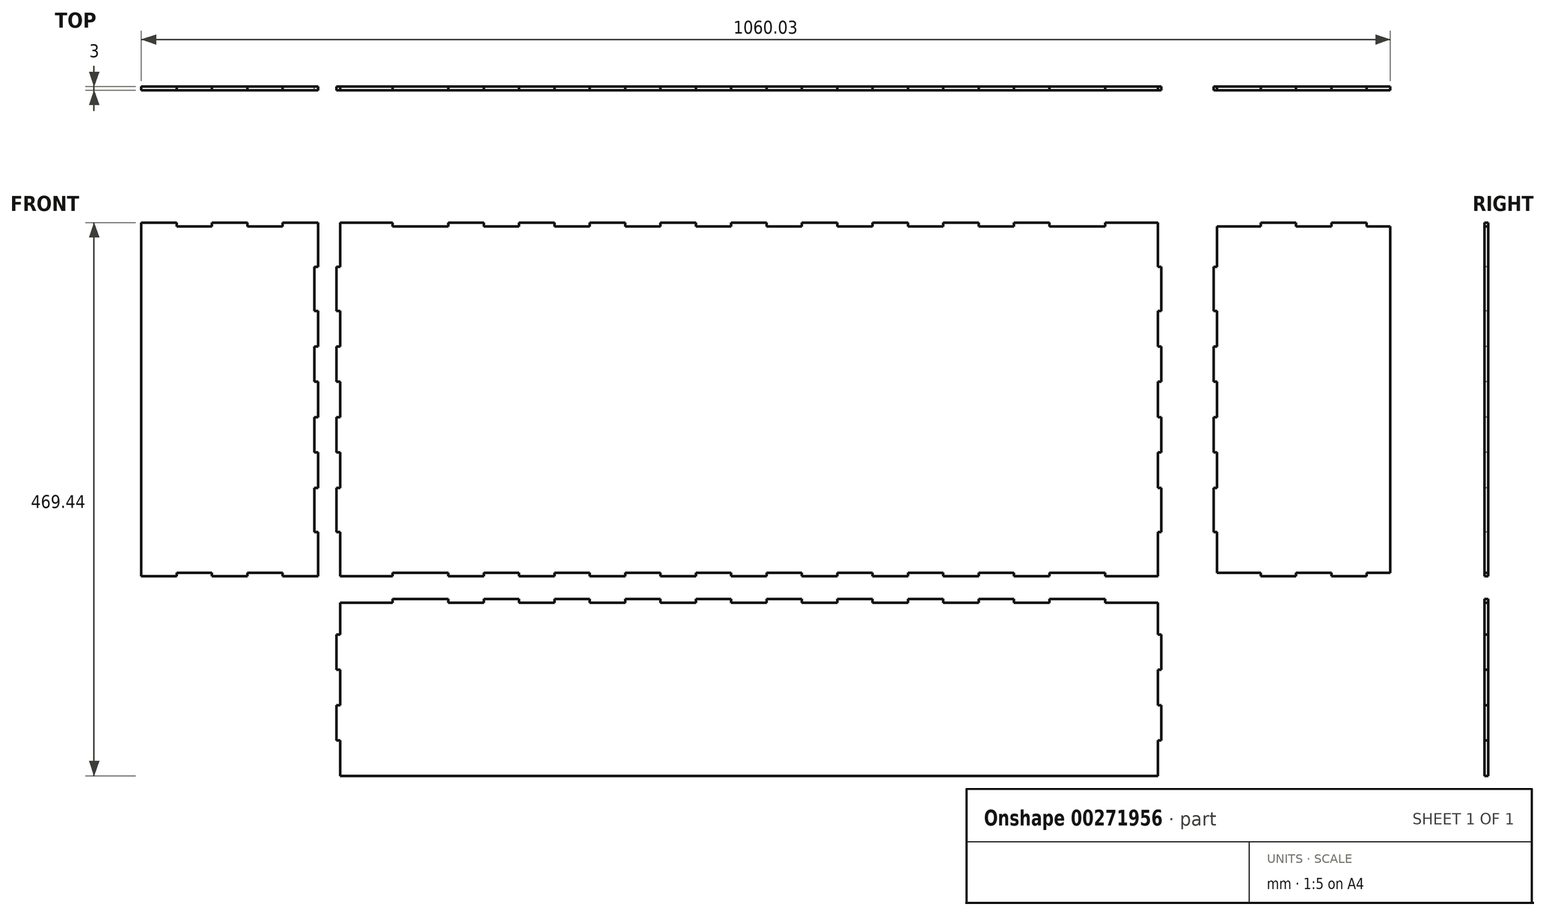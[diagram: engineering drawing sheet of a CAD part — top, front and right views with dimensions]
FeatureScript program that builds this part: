
annotation { "Feature Type Name" : "Feature", "Feature Type Description" : "" }
export const myFeature = defineFeature(function(context is Context, id is Id, definition is map)
    precondition{}
    {
        {
            var Q0;
            Q0=qCreatedBy(makeId("Front.planeOp"),FACE);
            var sketch = newSketch(context, id + "F0", { "sketchPlane" : qUnion([Q0])});
            skLineSegment(sketch, "E0", {"start": v(-432.84, 234.72) * mm, "end": v(-402.84, 234.72) * mm});
            skLineSegment(sketch, "E1", {"start": v(-402.84, 234.72) * mm, "end": v(-402.84, 231.72) * mm});
            skLineSegment(sketch, "E2", {"start": v(-402.84, 231.72) * mm, "end": v(-372.84, 231.72) * mm});
            skLineSegment(sketch, "E3", {"start": v(-372.84, 231.72) * mm, "end": v(-372.84, 234.72) * mm});
            skLineSegment(sketch, "E4", {"start": v(-372.84, 234.72) * mm, "end": v(-342.84, 234.72) * mm});
            skLineSegment(sketch, "E5", {"start": v(-342.84, 234.72) * mm, "end": v(-342.84, 231.72) * mm});
            skLineSegment(sketch, "E6", {"start": v(-342.84, 231.72) * mm, "end": v(-312.84, 231.72) * mm});
            skLineSegment(sketch, "E7", {"start": v(-312.84, 231.72) * mm, "end": v(-312.84, 234.72) * mm});
            skLineSegment(sketch, "E8", {"start": v(-312.84, 234.72) * mm, "end": v(-282.84, 234.72) * mm});
            skLineSegment(sketch, "E9", {"start": v(-282.84, 234.72) * mm, "end": v(-282.84, 197.22) * mm});
            skLineSegment(sketch, "E10", {"start": v(-282.84, 197.22) * mm, "end": v(-285.84, 197.22) * mm});
            skLineSegment(sketch, "E11", {"start": v(-285.84, 197.22) * mm, "end": v(-285.84, 159.72) * mm});
            skLineSegment(sketch, "E12", {"start": v(-285.84, 159.72) * mm, "end": v(-282.84, 159.72) * mm});
            skLineSegment(sketch, "E13", {"start": v(-282.84, 159.72) * mm, "end": v(-282.84, 129.72) * mm});
            skLineSegment(sketch, "E14", {"start": v(-282.84, 129.72) * mm, "end": v(-285.84, 129.72) * mm});
            skLineSegment(sketch, "E15", {"start": v(-285.84, 129.72) * mm, "end": v(-285.84, 99.72) * mm});
            skLineSegment(sketch, "E16", {"start": v(-285.84, 99.72) * mm, "end": v(-282.84, 99.72) * mm});
            skLineSegment(sketch, "E17", {"start": v(-282.84, 99.72) * mm, "end": v(-282.84, 69.72) * mm});
            skLineSegment(sketch, "E18", {"start": v(-282.84, 69.72) * mm, "end": v(-285.84, 69.72) * mm});
            skLineSegment(sketch, "E19", {"start": v(-285.84, 69.72) * mm, "end": v(-285.84, 39.72) * mm});
            skLineSegment(sketch, "E20", {"start": v(-285.84, 39.72) * mm, "end": v(-282.84, 39.72) * mm});
            skLineSegment(sketch, "E21", {"start": v(-282.84, 39.72) * mm, "end": v(-282.84, 9.72) * mm});
            skLineSegment(sketch, "E22", {"start": v(-282.84, 9.72) * mm, "end": v(-285.84, 9.72) * mm});
            skLineSegment(sketch, "E23", {"start": v(-285.84, 9.72) * mm, "end": v(-285.84, -27.78) * mm});
            skLineSegment(sketch, "E24", {"start": v(-285.84, -27.78) * mm, "end": v(-282.84, -27.78) * mm});
            skLineSegment(sketch, "E25", {"start": v(-282.84, -27.78) * mm, "end": v(-282.84, -65.28) * mm});
            skLineSegment(sketch, "E26", {"start": v(-282.84, -65.28) * mm, "end": v(-312.84, -65.28) * mm});
            skLineSegment(sketch, "E27", {"start": v(-312.84, -65.28) * mm, "end": v(-312.84, -62.28) * mm});
            skLineSegment(sketch, "E28", {"start": v(-312.84, -62.28) * mm, "end": v(-342.84, -62.28) * mm});
            skLineSegment(sketch, "E29", {"start": v(-342.84, -62.28) * mm, "end": v(-342.84, -65.28) * mm});
            skLineSegment(sketch, "E30", {"start": v(-342.84, -65.28) * mm, "end": v(-372.84, -65.28) * mm});
            skLineSegment(sketch, "E31", {"start": v(-372.84, -65.28) * mm, "end": v(-372.84, -62.28) * mm});
            skLineSegment(sketch, "E32", {"start": v(-372.84, -62.28) * mm, "end": v(-402.84, -62.28) * mm});
            skLineSegment(sketch, "E33", {"start": v(-402.84, -62.28) * mm, "end": v(-402.84, -65.28) * mm});
            skLineSegment(sketch, "E34", {"start": v(-402.84, -65.28) * mm, "end": v(-432.84, -65.28) * mm});
            skLineSegment(sketch, "E35", {"start": v(-432.84, -65.28) * mm, "end": v(-432.84, -27.78) * mm});
            skLineSegment(sketch, "E36", {"start": v(-432.84, -27.78) * mm, "end": v(-429.84, -27.78) * mm});
            skLineSegment(sketch, "E37", {"start": v(-429.84, -27.78) * mm, "end": v(-429.84, 9.72) * mm});
            skLineSegment(sketch, "E38", {"start": v(-429.84, 9.72) * mm, "end": v(-432.84, 9.72) * mm});
            skLineSegment(sketch, "E39", {"start": v(-432.84, 9.72) * mm, "end": v(-432.84, 39.72) * mm});
            skLineSegment(sketch, "E40", {"start": v(-432.84, 39.72) * mm, "end": v(-429.84, 39.72) * mm});
            skLineSegment(sketch, "E41", {"start": v(-429.84, 39.72) * mm, "end": v(-429.84, 69.72) * mm});
            skLineSegment(sketch, "E42", {"start": v(-429.84, 69.72) * mm, "end": v(-432.84, 69.72) * mm});
            skLineSegment(sketch, "E43", {"start": v(-432.84, 69.72) * mm, "end": v(-432.84, 99.72) * mm});
            skLineSegment(sketch, "E44", {"start": v(-432.84, 99.72) * mm, "end": v(-429.84, 99.72) * mm});
            skLineSegment(sketch, "E45", {"start": v(-429.84, 99.72) * mm, "end": v(-429.84, 129.72) * mm});
            skLineSegment(sketch, "E46", {"start": v(-429.84, 129.72) * mm, "end": v(-432.84, 129.72) * mm});
            skLineSegment(sketch, "E47", {"start": v(-432.84, 129.72) * mm, "end": v(-432.84, 159.72) * mm});
            skLineSegment(sketch, "E48", {"start": v(-432.84, 159.72) * mm, "end": v(-429.84, 159.72) * mm});
            skLineSegment(sketch, "E49", {"start": v(-429.84, 159.72) * mm, "end": v(-429.84, 197.22) * mm});
            skLineSegment(sketch, "E50", {"start": v(-429.84, 197.22) * mm, "end": v(-432.84, 197.22) * mm});
            skLineSegment(sketch, "E51", {"start": v(-432.84, 197.22) * mm, "end": v(-432.84, 234.72) * mm});
            skLineSegment(sketch, "E52", {"start": v(-264.16, 234.72) * mm, "end": v(-219.66, 234.72) * mm});
            skLineSegment(sketch, "E53", {"start": v(-219.66, 234.72) * mm, "end": v(-219.66, 231.72) * mm});
            skLineSegment(sketch, "E54", {"start": v(-219.66, 231.72) * mm, "end": v(-172.16, 231.72) * mm});
            skLineSegment(sketch, "E55", {"start": v(-172.16, 231.72) * mm, "end": v(-172.16, 234.72) * mm});
            skLineSegment(sketch, "E56", {"start": v(-172.16, 234.72) * mm, "end": v(-142.16, 234.72) * mm});
            skLineSegment(sketch, "E57", {"start": v(-142.16, 234.72) * mm, "end": v(-142.16, 231.72) * mm});
            skLineSegment(sketch, "E58", {"start": v(-142.16, 231.72) * mm, "end": v(-112.16, 231.72) * mm});
            skLineSegment(sketch, "E59", {"start": v(-112.16, 231.72) * mm, "end": v(-112.16, 234.72) * mm});
            skLineSegment(sketch, "E60", {"start": v(-112.16, 234.72) * mm, "end": v(-82.16, 234.72) * mm});
            skLineSegment(sketch, "E61", {"start": v(-82.16, 234.72) * mm, "end": v(-82.16, 231.72) * mm});
            skLineSegment(sketch, "E62", {"start": v(-82.16, 231.72) * mm, "end": v(-52.16, 231.72) * mm});
            skLineSegment(sketch, "E63", {"start": v(-52.16, 231.72) * mm, "end": v(-52.16, 234.72) * mm});
            skLineSegment(sketch, "E64", {"start": v(-52.16, 234.72) * mm, "end": v(-22.16, 234.72) * mm});
            skLineSegment(sketch, "E65", {"start": v(-22.16, 234.72) * mm, "end": v(-22.16, 231.72) * mm});
            skLineSegment(sketch, "E66", {"start": v(-22.16, 231.72) * mm, "end": v(7.84, 231.72) * mm});
            skLineSegment(sketch, "E67", {"start": v(7.84, 231.72) * mm, "end": v(7.84, 234.72) * mm});
            skLineSegment(sketch, "E68", {"start": v(7.84, 234.72) * mm, "end": v(37.84, 234.72) * mm});
            skLineSegment(sketch, "E69", {"start": v(37.84, 234.72) * mm, "end": v(37.84, 231.72) * mm});
            skLineSegment(sketch, "E70", {"start": v(37.84, 231.72) * mm, "end": v(67.84, 231.72) * mm});
            skLineSegment(sketch, "E71", {"start": v(67.84, 231.72) * mm, "end": v(67.84, 234.72) * mm});
            skLineSegment(sketch, "E72", {"start": v(67.84, 234.72) * mm, "end": v(97.84, 234.72) * mm});
            skLineSegment(sketch, "E73", {"start": v(97.84, 234.72) * mm, "end": v(97.84, 231.72) * mm});
            skLineSegment(sketch, "E74", {"start": v(97.84, 231.72) * mm, "end": v(127.84, 231.72) * mm});
            skLineSegment(sketch, "E75", {"start": v(127.84, 231.72) * mm, "end": v(127.84, 234.72) * mm});
            skLineSegment(sketch, "E76", {"start": v(127.84, 234.72) * mm, "end": v(157.84, 234.72) * mm});
            skLineSegment(sketch, "E77", {"start": v(157.84, 234.72) * mm, "end": v(157.84, 231.72) * mm});
            skLineSegment(sketch, "E78", {"start": v(157.84, 231.72) * mm, "end": v(187.84, 231.72) * mm});
            skLineSegment(sketch, "E79", {"start": v(187.84, 231.72) * mm, "end": v(187.84, 234.72) * mm});
            skLineSegment(sketch, "E80", {"start": v(187.84, 234.72) * mm, "end": v(217.84, 234.72) * mm});
            skLineSegment(sketch, "E81", {"start": v(217.84, 234.72) * mm, "end": v(217.84, 231.72) * mm});
            skLineSegment(sketch, "E82", {"start": v(217.84, 231.72) * mm, "end": v(247.84, 231.72) * mm});
            skLineSegment(sketch, "E83", {"start": v(247.84, 231.72) * mm, "end": v(247.84, 234.72) * mm});
            skLineSegment(sketch, "E84", {"start": v(247.84, 234.72) * mm, "end": v(277.84, 234.72) * mm});
            skLineSegment(sketch, "E85", {"start": v(277.84, 234.72) * mm, "end": v(277.84, 231.72) * mm});
            skLineSegment(sketch, "E86", {"start": v(277.84, 231.72) * mm, "end": v(307.84, 231.72) * mm});
            skLineSegment(sketch, "E87", {"start": v(307.84, 231.72) * mm, "end": v(307.84, 234.72) * mm});
            skLineSegment(sketch, "E88", {"start": v(307.84, 234.72) * mm, "end": v(337.84, 234.72) * mm});
            skLineSegment(sketch, "E89", {"start": v(337.84, 234.72) * mm, "end": v(337.84, 231.72) * mm});
            skLineSegment(sketch, "E90", {"start": v(337.84, 231.72) * mm, "end": v(385.34, 231.72) * mm});
            skLineSegment(sketch, "E91", {"start": v(385.34, 231.72) * mm, "end": v(385.34, 234.72) * mm});
            skLineSegment(sketch, "E92", {"start": v(385.34, 234.72) * mm, "end": v(429.84, 234.72) * mm});
            skLineSegment(sketch, "E93", {"start": v(429.84, 234.72) * mm, "end": v(429.84, 197.22) * mm});
            skLineSegment(sketch, "E94", {"start": v(429.84, 197.22) * mm, "end": v(432.84, 197.22) * mm});
            skLineSegment(sketch, "E95", {"start": v(432.84, 197.22) * mm, "end": v(432.84, 159.72) * mm});
            skLineSegment(sketch, "E96", {"start": v(432.84, 159.72) * mm, "end": v(429.84, 159.72) * mm});
            skLineSegment(sketch, "E97", {"start": v(429.84, 159.72) * mm, "end": v(429.84, 129.72) * mm});
            skLineSegment(sketch, "E98", {"start": v(429.84, 129.72) * mm, "end": v(432.84, 129.72) * mm});
            skLineSegment(sketch, "E99", {"start": v(432.84, 129.72) * mm, "end": v(432.84, 99.72) * mm});
            skLineSegment(sketch, "E100", {"start": v(432.84, 99.72) * mm, "end": v(429.84, 99.72) * mm});
            skLineSegment(sketch, "E101", {"start": v(429.84, 99.72) * mm, "end": v(429.84, 69.72) * mm});
            skLineSegment(sketch, "E102", {"start": v(429.84, 69.72) * mm, "end": v(432.84, 69.72) * mm});
            skLineSegment(sketch, "E103", {"start": v(432.84, 69.72) * mm, "end": v(432.84, 39.72) * mm});
            skLineSegment(sketch, "E104", {"start": v(432.84, 39.72) * mm, "end": v(429.84, 39.72) * mm});
            skLineSegment(sketch, "E105", {"start": v(429.84, 39.72) * mm, "end": v(429.84, 9.72) * mm});
            skLineSegment(sketch, "E106", {"start": v(429.84, 9.72) * mm, "end": v(432.84, 9.72) * mm});
            skLineSegment(sketch, "E107", {"start": v(432.84, 9.72) * mm, "end": v(432.84, -27.78) * mm});
            skLineSegment(sketch, "E108", {"start": v(432.84, -27.78) * mm, "end": v(429.84, -27.78) * mm});
            skLineSegment(sketch, "E109", {"start": v(429.84, -27.78) * mm, "end": v(429.84, -65.28) * mm});
            skLineSegment(sketch, "E110", {"start": v(429.84, -65.28) * mm, "end": v(385.34, -65.28) * mm});
            skLineSegment(sketch, "E111", {"start": v(385.34, -65.28) * mm, "end": v(385.34, -62.28) * mm});
            skLineSegment(sketch, "E112", {"start": v(385.34, -62.28) * mm, "end": v(337.84, -62.28) * mm});
            skLineSegment(sketch, "E113", {"start": v(337.84, -62.28) * mm, "end": v(337.84, -65.28) * mm});
            skLineSegment(sketch, "E114", {"start": v(337.84, -65.28) * mm, "end": v(307.84, -65.28) * mm});
            skLineSegment(sketch, "E115", {"start": v(307.84, -65.28) * mm, "end": v(307.84, -62.28) * mm});
            skLineSegment(sketch, "E116", {"start": v(307.84, -62.28) * mm, "end": v(277.84, -62.28) * mm});
            skLineSegment(sketch, "E117", {"start": v(277.84, -62.28) * mm, "end": v(277.84, -65.28) * mm});
            skLineSegment(sketch, "E118", {"start": v(277.84, -65.28) * mm, "end": v(247.84, -65.28) * mm});
            skLineSegment(sketch, "E119", {"start": v(247.84, -65.28) * mm, "end": v(247.84, -62.28) * mm});
            skLineSegment(sketch, "E120", {"start": v(247.84, -62.28) * mm, "end": v(217.84, -62.28) * mm});
            skLineSegment(sketch, "E121", {"start": v(217.84, -62.28) * mm, "end": v(217.84, -65.28) * mm});
            skLineSegment(sketch, "E122", {"start": v(217.84, -65.28) * mm, "end": v(187.84, -65.28) * mm});
            skLineSegment(sketch, "E123", {"start": v(187.84, -65.28) * mm, "end": v(187.84, -62.28) * mm});
            skLineSegment(sketch, "E124", {"start": v(187.84, -62.28) * mm, "end": v(157.84, -62.28) * mm});
            skLineSegment(sketch, "E125", {"start": v(157.84, -62.28) * mm, "end": v(157.84, -65.28) * mm});
            skLineSegment(sketch, "E126", {"start": v(157.84, -65.28) * mm, "end": v(127.84, -65.28) * mm});
            skLineSegment(sketch, "E127", {"start": v(127.84, -65.28) * mm, "end": v(127.84, -62.28) * mm});
            skLineSegment(sketch, "E128", {"start": v(127.84, -62.28) * mm, "end": v(97.84, -62.28) * mm});
            skLineSegment(sketch, "E129", {"start": v(97.84, -62.28) * mm, "end": v(97.84, -65.28) * mm});
            skLineSegment(sketch, "E130", {"start": v(97.84, -65.28) * mm, "end": v(67.84, -65.28) * mm});
            skLineSegment(sketch, "E131", {"start": v(67.84, -65.28) * mm, "end": v(67.84, -62.28) * mm});
            skLineSegment(sketch, "E132", {"start": v(67.84, -62.28) * mm, "end": v(37.84, -62.28) * mm});
            skLineSegment(sketch, "E133", {"start": v(37.84, -62.28) * mm, "end": v(37.84, -65.28) * mm});
            skLineSegment(sketch, "E134", {"start": v(37.84, -65.28) * mm, "end": v(7.84, -65.28) * mm});
            skLineSegment(sketch, "E135", {"start": v(7.84, -65.28) * mm, "end": v(7.84, -62.28) * mm});
            skLineSegment(sketch, "E136", {"start": v(7.84, -62.28) * mm, "end": v(-22.16, -62.28) * mm});
            skLineSegment(sketch, "E137", {"start": v(-22.16, -62.28) * mm, "end": v(-22.16, -65.28) * mm});
            skLineSegment(sketch, "E138", {"start": v(-22.16, -65.28) * mm, "end": v(-52.16, -65.28) * mm});
            skLineSegment(sketch, "E139", {"start": v(-52.16, -65.28) * mm, "end": v(-52.16, -62.28) * mm});
            skLineSegment(sketch, "E140", {"start": v(-52.16, -62.28) * mm, "end": v(-82.16, -62.28) * mm});
            skLineSegment(sketch, "E141", {"start": v(-82.16, -62.28) * mm, "end": v(-82.16, -65.28) * mm});
            skLineSegment(sketch, "E142", {"start": v(-82.16, -65.28) * mm, "end": v(-112.16, -65.28) * mm});
            skLineSegment(sketch, "E143", {"start": v(-112.16, -65.28) * mm, "end": v(-112.16, -62.28) * mm});
            skLineSegment(sketch, "E144", {"start": v(-112.16, -62.28) * mm, "end": v(-142.16, -62.28) * mm});
            skLineSegment(sketch, "E145", {"start": v(-142.16, -62.28) * mm, "end": v(-142.16, -65.28) * mm});
            skLineSegment(sketch, "E146", {"start": v(-142.16, -65.28) * mm, "end": v(-172.16, -65.28) * mm});
            skLineSegment(sketch, "E147", {"start": v(-172.16, -65.28) * mm, "end": v(-172.16, -62.28) * mm});
            skLineSegment(sketch, "E148", {"start": v(-172.16, -62.28) * mm, "end": v(-219.66, -62.28) * mm});
            skLineSegment(sketch, "E149", {"start": v(-219.66, -62.28) * mm, "end": v(-219.66, -65.28) * mm});
            skLineSegment(sketch, "E150", {"start": v(-219.66, -65.28) * mm, "end": v(-264.16, -65.28) * mm});
            skLineSegment(sketch, "E151", {"start": v(-264.16, -65.28) * mm, "end": v(-264.16, -27.78) * mm});
            skLineSegment(sketch, "E152", {"start": v(-264.16, -27.78) * mm, "end": v(-267.16, -27.78) * mm});
            skLineSegment(sketch, "E153", {"start": v(-267.16, -27.78) * mm, "end": v(-267.16, 9.72) * mm});
            skLineSegment(sketch, "E154", {"start": v(-267.16, 9.72) * mm, "end": v(-264.16, 9.72) * mm});
            skLineSegment(sketch, "E155", {"start": v(-264.16, 9.72) * mm, "end": v(-264.16, 39.72) * mm});
            skLineSegment(sketch, "E156", {"start": v(-264.16, 39.72) * mm, "end": v(-267.16, 39.72) * mm});
            skLineSegment(sketch, "E157", {"start": v(-267.16, 39.72) * mm, "end": v(-267.16, 69.72) * mm});
            skLineSegment(sketch, "E158", {"start": v(-267.16, 69.72) * mm, "end": v(-264.16, 69.72) * mm});
            skLineSegment(sketch, "E159", {"start": v(-264.16, 69.72) * mm, "end": v(-264.16, 99.72) * mm});
            skLineSegment(sketch, "E160", {"start": v(-264.16, 99.72) * mm, "end": v(-267.16, 99.72) * mm});
            skLineSegment(sketch, "E161", {"start": v(-267.16, 99.72) * mm, "end": v(-267.16, 129.72) * mm});
            skLineSegment(sketch, "E162", {"start": v(-267.16, 129.72) * mm, "end": v(-264.16, 129.72) * mm});
            skLineSegment(sketch, "E163", {"start": v(-264.16, 129.72) * mm, "end": v(-264.16, 159.72) * mm});
            skLineSegment(sketch, "E164", {"start": v(-264.16, 159.72) * mm, "end": v(-267.16, 159.72) * mm});
            skLineSegment(sketch, "E165", {"start": v(-267.16, 159.72) * mm, "end": v(-267.16, 197.22) * mm});
            skLineSegment(sketch, "E166", {"start": v(-267.16, 197.22) * mm, "end": v(-264.16, 197.22) * mm});
            skLineSegment(sketch, "E167", {"start": v(-264.16, 197.22) * mm, "end": v(-264.16, 234.72) * mm});
            skLineSegment(sketch, "E168", {"start": v(429.84, -87.72) * mm, "end": v(429.84, -114.72) * mm});
            skLineSegment(sketch, "E169", {"start": v(429.84, -114.72) * mm, "end": v(432.84, -114.72) * mm});
            skLineSegment(sketch, "E170", {"start": v(432.84, -114.72) * mm, "end": v(432.84, -144.72) * mm});
            skLineSegment(sketch, "E171", {"start": v(432.84, -144.72) * mm, "end": v(429.84, -144.72) * mm});
            skLineSegment(sketch, "E172", {"start": v(429.84, -144.72) * mm, "end": v(429.84, -174.72) * mm});
            skLineSegment(sketch, "E173", {"start": v(429.84, -174.72) * mm, "end": v(432.84, -174.72) * mm});
            skLineSegment(sketch, "E174", {"start": v(432.84, -174.72) * mm, "end": v(432.84, -204.72) * mm});
            skLineSegment(sketch, "E175", {"start": v(432.84, -204.72) * mm, "end": v(429.84, -204.72) * mm});
            skLineSegment(sketch, "E176", {"start": v(429.84, -204.72) * mm, "end": v(429.84, -231.72) * mm});
            skLineSegment(sketch, "E177", {"start": v(429.84, -231.72) * mm, "end": v(385.34, -231.72) * mm});
            skLineSegment(sketch, "E178", {"start": v(385.34, -231.72) * mm, "end": v(385.34, -234.72) * mm});
            skLineSegment(sketch, "E179", {"start": v(385.34, -234.72) * mm, "end": v(337.84, -234.72) * mm});
            skLineSegment(sketch, "E180", {"start": v(337.84, -234.72) * mm, "end": v(337.84, -231.72) * mm});
            skLineSegment(sketch, "E181", {"start": v(337.84, -231.72) * mm, "end": v(307.84, -231.72) * mm});
            skLineSegment(sketch, "E182", {"start": v(307.84, -231.72) * mm, "end": v(307.84, -234.72) * mm});
            skLineSegment(sketch, "E183", {"start": v(307.84, -234.72) * mm, "end": v(277.84, -234.72) * mm});
            skLineSegment(sketch, "E184", {"start": v(277.84, -234.72) * mm, "end": v(277.84, -231.72) * mm});
            skLineSegment(sketch, "E185", {"start": v(277.84, -231.72) * mm, "end": v(247.84, -231.72) * mm});
            skLineSegment(sketch, "E186", {"start": v(247.84, -231.72) * mm, "end": v(247.84, -234.72) * mm});
            skLineSegment(sketch, "E187", {"start": v(247.84, -234.72) * mm, "end": v(217.84, -234.72) * mm});
            skLineSegment(sketch, "E188", {"start": v(217.84, -234.72) * mm, "end": v(217.84, -231.72) * mm});
            skLineSegment(sketch, "E189", {"start": v(217.84, -231.72) * mm, "end": v(187.84, -231.72) * mm});
            skLineSegment(sketch, "E190", {"start": v(187.84, -231.72) * mm, "end": v(187.84, -234.72) * mm});
            skLineSegment(sketch, "E191", {"start": v(187.84, -234.72) * mm, "end": v(157.84, -234.72) * mm});
            skLineSegment(sketch, "E192", {"start": v(157.84, -234.72) * mm, "end": v(157.84, -231.72) * mm});
            skLineSegment(sketch, "E193", {"start": v(157.84, -231.72) * mm, "end": v(127.84, -231.72) * mm});
            skLineSegment(sketch, "E194", {"start": v(127.84, -231.72) * mm, "end": v(127.84, -234.72) * mm});
            skLineSegment(sketch, "E195", {"start": v(127.84, -234.72) * mm, "end": v(97.84, -234.72) * mm});
            skLineSegment(sketch, "E196", {"start": v(97.84, -234.72) * mm, "end": v(97.84, -231.72) * mm});
            skLineSegment(sketch, "E197", {"start": v(97.84, -231.72) * mm, "end": v(67.84, -231.72) * mm});
            skLineSegment(sketch, "E198", {"start": v(67.84, -231.72) * mm, "end": v(67.84, -234.72) * mm});
            skLineSegment(sketch, "E199", {"start": v(67.84, -234.72) * mm, "end": v(37.84, -234.72) * mm});
            skLineSegment(sketch, "E200", {"start": v(37.84, -234.72) * mm, "end": v(37.84, -231.72) * mm});
            skLineSegment(sketch, "E201", {"start": v(37.84, -231.72) * mm, "end": v(7.84, -231.72) * mm});
            skLineSegment(sketch, "E202", {"start": v(7.84, -231.72) * mm, "end": v(7.84, -234.72) * mm});
            skLineSegment(sketch, "E203", {"start": v(7.84, -234.72) * mm, "end": v(-22.16, -234.72) * mm});
            skLineSegment(sketch, "E204", {"start": v(-22.16, -234.72) * mm, "end": v(-22.16, -231.72) * mm});
            skLineSegment(sketch, "E205", {"start": v(-22.16, -231.72) * mm, "end": v(-52.16, -231.72) * mm});
            skLineSegment(sketch, "E206", {"start": v(-52.16, -231.72) * mm, "end": v(-52.16, -234.72) * mm});
            skLineSegment(sketch, "E207", {"start": v(-52.16, -234.72) * mm, "end": v(-82.16, -234.72) * mm});
            skLineSegment(sketch, "E208", {"start": v(-82.16, -234.72) * mm, "end": v(-82.16, -231.72) * mm});
            skLineSegment(sketch, "E209", {"start": v(-82.16, -231.72) * mm, "end": v(-112.16, -231.72) * mm});
            skLineSegment(sketch, "E210", {"start": v(-112.16, -231.72) * mm, "end": v(-112.16, -234.72) * mm});
            skLineSegment(sketch, "E211", {"start": v(-112.16, -234.72) * mm, "end": v(-142.16, -234.72) * mm});
            skLineSegment(sketch, "E212", {"start": v(-142.16, -234.72) * mm, "end": v(-142.16, -231.72) * mm});
            skLineSegment(sketch, "E213", {"start": v(-142.16, -231.72) * mm, "end": v(-172.16, -231.72) * mm});
            skLineSegment(sketch, "E214", {"start": v(-172.16, -231.72) * mm, "end": v(-172.16, -234.72) * mm});
            skLineSegment(sketch, "E215", {"start": v(-172.16, -234.72) * mm, "end": v(-219.66, -234.72) * mm});
            skLineSegment(sketch, "E216", {"start": v(-219.66, -234.72) * mm, "end": v(-219.66, -231.72) * mm});
            skLineSegment(sketch, "E217", {"start": v(-219.66, -231.72) * mm, "end": v(-264.16, -231.72) * mm});
            skLineSegment(sketch, "E218", {"start": v(-264.16, -231.72) * mm, "end": v(-264.16, -204.72) * mm});
            skLineSegment(sketch, "E219", {"start": v(-264.16, -204.72) * mm, "end": v(-267.16, -204.72) * mm});
            skLineSegment(sketch, "E220", {"start": v(-267.16, -204.72) * mm, "end": v(-267.16, -174.72) * mm});
            skLineSegment(sketch, "E221", {"start": v(-267.16, -174.72) * mm, "end": v(-264.16, -174.72) * mm});
            skLineSegment(sketch, "E222", {"start": v(-264.16, -174.72) * mm, "end": v(-264.16, -144.72) * mm});
            skLineSegment(sketch, "E223", {"start": v(-264.16, -144.72) * mm, "end": v(-267.16, -144.72) * mm});
            skLineSegment(sketch, "E224", {"start": v(-267.16, -144.72) * mm, "end": v(-267.16, -114.72) * mm});
            skLineSegment(sketch, "E225", {"start": v(-267.16, -114.72) * mm, "end": v(-264.16, -114.72) * mm});
            skLineSegment(sketch, "E226", {"start": v(-264.16, -114.72) * mm, "end": v(-264.16, -87.72) * mm});
            skLineSegment(sketch, "E227", {"start": v(-264.16, -87.72) * mm, "end": v(-219.66, -87.72) * mm});
            skLineSegment(sketch, "E228", {"start": v(-219.66, -87.72) * mm, "end": v(-219.66, -84.72) * mm});
            skLineSegment(sketch, "E229", {"start": v(-219.66, -84.72) * mm, "end": v(-172.16, -84.72) * mm});
            skLineSegment(sketch, "E230", {"start": v(-172.16, -84.72) * mm, "end": v(-172.16, -87.72) * mm});
            skLineSegment(sketch, "E231", {"start": v(-172.16, -87.72) * mm, "end": v(-142.16, -87.72) * mm});
            skLineSegment(sketch, "E232", {"start": v(-142.16, -87.72) * mm, "end": v(-142.16, -84.72) * mm});
            skLineSegment(sketch, "E233", {"start": v(-142.16, -84.72) * mm, "end": v(-112.16, -84.72) * mm});
            skLineSegment(sketch, "E234", {"start": v(-112.16, -84.72) * mm, "end": v(-112.16, -87.72) * mm});
            skLineSegment(sketch, "E235", {"start": v(-112.16, -87.72) * mm, "end": v(-82.16, -87.72) * mm});
            skLineSegment(sketch, "E236", {"start": v(-82.16, -87.72) * mm, "end": v(-82.16, -84.72) * mm});
            skLineSegment(sketch, "E237", {"start": v(-82.16, -84.72) * mm, "end": v(-52.16, -84.72) * mm});
            skLineSegment(sketch, "E238", {"start": v(-52.16, -84.72) * mm, "end": v(-52.16, -87.72) * mm});
            skLineSegment(sketch, "E239", {"start": v(-52.16, -87.72) * mm, "end": v(-22.16, -87.72) * mm});
            skLineSegment(sketch, "E240", {"start": v(-22.16, -87.72) * mm, "end": v(-22.16, -84.72) * mm});
            skLineSegment(sketch, "E241", {"start": v(-22.16, -84.72) * mm, "end": v(7.84, -84.72) * mm});
            skLineSegment(sketch, "E242", {"start": v(7.84, -84.72) * mm, "end": v(7.84, -87.72) * mm});
            skLineSegment(sketch, "E243", {"start": v(7.84, -87.72) * mm, "end": v(37.84, -87.72) * mm});
            skLineSegment(sketch, "E244", {"start": v(37.84, -87.72) * mm, "end": v(37.84, -84.72) * mm});
            skLineSegment(sketch, "E245", {"start": v(37.84, -84.72) * mm, "end": v(67.84, -84.72) * mm});
            skLineSegment(sketch, "E246", {"start": v(67.84, -84.72) * mm, "end": v(67.84, -87.72) * mm});
            skLineSegment(sketch, "E247", {"start": v(67.84, -87.72) * mm, "end": v(97.84, -87.72) * mm});
            skLineSegment(sketch, "E248", {"start": v(97.84, -87.72) * mm, "end": v(97.84, -84.72) * mm});
            skLineSegment(sketch, "E249", {"start": v(97.84, -84.72) * mm, "end": v(127.84, -84.72) * mm});
            skLineSegment(sketch, "E250", {"start": v(127.84, -84.72) * mm, "end": v(127.84, -87.72) * mm});
            skLineSegment(sketch, "E251", {"start": v(127.84, -87.72) * mm, "end": v(157.84, -87.72) * mm});
            skLineSegment(sketch, "E252", {"start": v(157.84, -87.72) * mm, "end": v(157.84, -84.72) * mm});
            skLineSegment(sketch, "E253", {"start": v(157.84, -84.72) * mm, "end": v(187.84, -84.72) * mm});
            skLineSegment(sketch, "E254", {"start": v(187.84, -84.72) * mm, "end": v(187.84, -87.72) * mm});
            skLineSegment(sketch, "E255", {"start": v(187.84, -87.72) * mm, "end": v(217.84, -87.72) * mm});
            skLineSegment(sketch, "E256", {"start": v(217.84, -87.72) * mm, "end": v(217.84, -84.72) * mm});
            skLineSegment(sketch, "E257", {"start": v(217.84, -84.72) * mm, "end": v(247.84, -84.72) * mm});
            skLineSegment(sketch, "E258", {"start": v(247.84, -84.72) * mm, "end": v(247.84, -87.72) * mm});
            skLineSegment(sketch, "E259", {"start": v(247.84, -87.72) * mm, "end": v(277.84, -87.72) * mm});
            skLineSegment(sketch, "E260", {"start": v(277.84, -87.72) * mm, "end": v(277.84, -84.72) * mm});
            skLineSegment(sketch, "E261", {"start": v(277.84, -84.72) * mm, "end": v(307.84, -84.72) * mm});
            skLineSegment(sketch, "E262", {"start": v(307.84, -84.72) * mm, "end": v(307.84, -87.72) * mm});
            skLineSegment(sketch, "E263", {"start": v(307.84, -87.72) * mm, "end": v(337.84, -87.72) * mm});
            skLineSegment(sketch, "E264", {"start": v(337.84, -87.72) * mm, "end": v(337.84, -84.72) * mm});
            skLineSegment(sketch, "E265", {"start": v(337.84, -84.72) * mm, "end": v(385.34, -84.72) * mm});
            skLineSegment(sketch, "E266", {"start": v(385.34, -84.72) * mm, "end": v(385.34, -87.72) * mm});
            skLineSegment(sketch, "E267", {"start": v(385.34, -87.72) * mm, "end": v(429.84, -87.72) * mm});
            skSolve(sketch);
        }
        {
            var Q0;
            Q0 = qSketchRegion(id + "F0", true);
            extrude(context, id + "F1", {"entities" : qUnion([Q0]), "depth" : 3 * mm});
        }
        {
            var Q0;
            Q0=makeQuery(id+"F1.opExtrude","CAP_FACE",FACE,{"disambiguationData":[OSD([sQuery(id+"F0.wireOp",EDGE,"E0"),sQuery(id+"F0.wireOp",EDGE,"E1"),sQuery(id+"F0.wireOp",EDGE,"E2"),sQuery(id+"F0.wireOp",EDGE,"E3"),sQuery(id+"F0.wireOp",EDGE,"E4"),sQuery(id+"F0.wireOp",EDGE,"E5"),sQuery(id+"F0.wireOp",EDGE,"E6"),sQuery(id+"F0.wireOp",EDGE,"E7"),sQuery(id+"F0.wireOp",EDGE,"E8"),sQuery(id+"F0.wireOp",EDGE,"E9"),sQuery(id+"F0.wireOp",EDGE,"E10"),sQuery(id+"F0.wireOp",EDGE,"E11"),sQuery(id+"F0.wireOp",EDGE,"E12"),sQuery(id+"F0.wireOp",EDGE,"E13"),sQuery(id+"F0.wireOp",EDGE,"E14"),sQuery(id+"F0.wireOp",EDGE,"E15"),sQuery(id+"F0.wireOp",EDGE,"E16"),sQuery(id+"F0.wireOp",EDGE,"E17"),sQuery(id+"F0.wireOp",EDGE,"E18"),sQuery(id+"F0.wireOp",EDGE,"E19"),sQuery(id+"F0.wireOp",EDGE,"E20"),sQuery(id+"F0.wireOp",EDGE,"E21"),sQuery(id+"F0.wireOp",EDGE,"E22"),sQuery(id+"F0.wireOp",EDGE,"E23"),sQuery(id+"F0.wireOp",EDGE,"E24"),sQuery(id+"F0.wireOp",EDGE,"E25"),sQuery(id+"F0.wireOp",EDGE,"E26"),sQuery(id+"F0.wireOp",EDGE,"E27"),sQuery(id+"F0.wireOp",EDGE,"E28"),sQuery(id+"F0.wireOp",EDGE,"E29"),sQuery(id+"F0.wireOp",EDGE,"E30"),sQuery(id+"F0.wireOp",EDGE,"E31"),sQuery(id+"F0.wireOp",EDGE,"E32"),sQuery(id+"F0.wireOp",EDGE,"E33"),sQuery(id+"F0.wireOp",EDGE,"E34"),sQuery(id+"F0.wireOp",EDGE,"E35"),sQuery(id+"F0.wireOp",EDGE,"E36"),sQuery(id+"F0.wireOp",EDGE,"E37"),sQuery(id+"F0.wireOp",EDGE,"E38"),sQuery(id+"F0.wireOp",EDGE,"E39"),sQuery(id+"F0.wireOp",EDGE,"E40"),sQuery(id+"F0.wireOp",EDGE,"E41"),sQuery(id+"F0.wireOp",EDGE,"E42"),sQuery(id+"F0.wireOp",EDGE,"E43"),sQuery(id+"F0.wireOp",EDGE,"E44"),sQuery(id+"F0.wireOp",EDGE,"E45"),sQuery(id+"F0.wireOp",EDGE,"E46"),sQuery(id+"F0.wireOp",EDGE,"E47"),sQuery(id+"F0.wireOp",EDGE,"E48"),sQuery(id+"F0.wireOp",EDGE,"E49"),sQuery(id+"F0.wireOp",EDGE,"E50"),sQuery(id+"F0.wireOp",EDGE,"E51")])],"isStart":false});
            var sketch = newSketch(context, id + "F2", { "sketchPlane" : qUnion([Q0])});
            skLineSegment(sketch, "E268.bottom", {"start": v(-432.84, 197.22) * mm, "end": v(-429.84, 197.22) * mm});
            skLineSegment(sketch, "E268.top", {"start": v(-432.84, -27.78) * mm, "end": v(-429.84, -27.78) * mm});
            skLineSegment(sketch, "E268.left", {"start": v(-432.84, 197.22) * mm, "end": v(-432.84, -27.78) * mm});
            skLineSegment(sketch, "E268.right", {"start": v(-429.84, 197.22) * mm, "end": v(-429.84, -27.78) * mm});
            skSolve(sketch);
        }
        {
            var Q0;
            Q0 = qSketchRegion(id + "F2", true);
            extrude(context, id + "F3", {"entities" : qUnion([Q0]), "operationType" : NewBodyOperationType.ADD, "oppositeDirection" : true, "depth" : 3 * mm});
        }
        {
            var Q0;
            Q0=makeQuery(id+"F1.opExtrude","CAP_FACE",FACE,{"disambiguationData":[OSD([sQuery(id+"F0.wireOp",EDGE,"E168"),sQuery(id+"F0.wireOp",EDGE,"E169"),sQuery(id+"F0.wireOp",EDGE,"E170"),sQuery(id+"F0.wireOp",EDGE,"E171"),sQuery(id+"F0.wireOp",EDGE,"E172"),sQuery(id+"F0.wireOp",EDGE,"E173"),sQuery(id+"F0.wireOp",EDGE,"E174"),sQuery(id+"F0.wireOp",EDGE,"E175"),sQuery(id+"F0.wireOp",EDGE,"E176"),sQuery(id+"F0.wireOp",EDGE,"E177"),sQuery(id+"F0.wireOp",EDGE,"E178"),sQuery(id+"F0.wireOp",EDGE,"E179"),sQuery(id+"F0.wireOp",EDGE,"E180"),sQuery(id+"F0.wireOp",EDGE,"E181"),sQuery(id+"F0.wireOp",EDGE,"E182"),sQuery(id+"F0.wireOp",EDGE,"E183"),sQuery(id+"F0.wireOp",EDGE,"E184"),sQuery(id+"F0.wireOp",EDGE,"E185"),sQuery(id+"F0.wireOp",EDGE,"E186"),sQuery(id+"F0.wireOp",EDGE,"E187"),sQuery(id+"F0.wireOp",EDGE,"E188"),sQuery(id+"F0.wireOp",EDGE,"E189"),sQuery(id+"F0.wireOp",EDGE,"E190"),sQuery(id+"F0.wireOp",EDGE,"E191"),sQuery(id+"F0.wireOp",EDGE,"E192"),sQuery(id+"F0.wireOp",EDGE,"E193"),sQuery(id+"F0.wireOp",EDGE,"E194"),sQuery(id+"F0.wireOp",EDGE,"E195"),sQuery(id+"F0.wireOp",EDGE,"E196"),sQuery(id+"F0.wireOp",EDGE,"E197"),sQuery(id+"F0.wireOp",EDGE,"E198"),sQuery(id+"F0.wireOp",EDGE,"E199"),sQuery(id+"F0.wireOp",EDGE,"E200"),sQuery(id+"F0.wireOp",EDGE,"E201"),sQuery(id+"F0.wireOp",EDGE,"E202"),sQuery(id+"F0.wireOp",EDGE,"E203"),sQuery(id+"F0.wireOp",EDGE,"E204"),sQuery(id+"F0.wireOp",EDGE,"E205"),sQuery(id+"F0.wireOp",EDGE,"E206"),sQuery(id+"F0.wireOp",EDGE,"E207"),sQuery(id+"F0.wireOp",EDGE,"E208"),sQuery(id+"F0.wireOp",EDGE,"E209"),sQuery(id+"F0.wireOp",EDGE,"E210"),sQuery(id+"F0.wireOp",EDGE,"E211"),sQuery(id+"F0.wireOp",EDGE,"E212"),sQuery(id+"F0.wireOp",EDGE,"E213"),sQuery(id+"F0.wireOp",EDGE,"E214"),sQuery(id+"F0.wireOp",EDGE,"E215"),sQuery(id+"F0.wireOp",EDGE,"E216"),sQuery(id+"F0.wireOp",EDGE,"E217"),sQuery(id+"F0.wireOp",EDGE,"E218"),sQuery(id+"F0.wireOp",EDGE,"E219"),sQuery(id+"F0.wireOp",EDGE,"E220"),sQuery(id+"F0.wireOp",EDGE,"E221"),sQuery(id+"F0.wireOp",EDGE,"E222"),sQuery(id+"F0.wireOp",EDGE,"E223"),sQuery(id+"F0.wireOp",EDGE,"E224"),sQuery(id+"F0.wireOp",EDGE,"E225"),sQuery(id+"F0.wireOp",EDGE,"E226"),sQuery(id+"F0.wireOp",EDGE,"E227"),sQuery(id+"F0.wireOp",EDGE,"E228"),sQuery(id+"F0.wireOp",EDGE,"E229"),sQuery(id+"F0.wireOp",EDGE,"E230"),sQuery(id+"F0.wireOp",EDGE,"E231"),sQuery(id+"F0.wireOp",EDGE,"E232"),sQuery(id+"F0.wireOp",EDGE,"E233"),sQuery(id+"F0.wireOp",EDGE,"E234"),sQuery(id+"F0.wireOp",EDGE,"E235"),sQuery(id+"F0.wireOp",EDGE,"E236"),sQuery(id+"F0.wireOp",EDGE,"E237"),sQuery(id+"F0.wireOp",EDGE,"E238"),sQuery(id+"F0.wireOp",EDGE,"E239"),sQuery(id+"F0.wireOp",EDGE,"E240"),sQuery(id+"F0.wireOp",EDGE,"E241"),sQuery(id+"F0.wireOp",EDGE,"E242"),sQuery(id+"F0.wireOp",EDGE,"E243"),sQuery(id+"F0.wireOp",EDGE,"E244"),sQuery(id+"F0.wireOp",EDGE,"E245"),sQuery(id+"F0.wireOp",EDGE,"E246"),sQuery(id+"F0.wireOp",EDGE,"E247"),sQuery(id+"F0.wireOp",EDGE,"E248"),sQuery(id+"F0.wireOp",EDGE,"E249"),sQuery(id+"F0.wireOp",EDGE,"E250"),sQuery(id+"F0.wireOp",EDGE,"E251"),sQuery(id+"F0.wireOp",EDGE,"E252"),sQuery(id+"F0.wireOp",EDGE,"E253"),sQuery(id+"F0.wireOp",EDGE,"E254"),sQuery(id+"F0.wireOp",EDGE,"E255"),sQuery(id+"F0.wireOp",EDGE,"E256"),sQuery(id+"F0.wireOp",EDGE,"E257"),sQuery(id+"F0.wireOp",EDGE,"E258"),sQuery(id+"F0.wireOp",EDGE,"E259"),sQuery(id+"F0.wireOp",EDGE,"E260"),sQuery(id+"F0.wireOp",EDGE,"E261"),sQuery(id+"F0.wireOp",EDGE,"E262"),sQuery(id+"F0.wireOp",EDGE,"E263"),sQuery(id+"F0.wireOp",EDGE,"E264"),sQuery(id+"F0.wireOp",EDGE,"E265"),sQuery(id+"F0.wireOp",EDGE,"E266"),sQuery(id+"F0.wireOp",EDGE,"E267")])],"isStart":false});
            var sketch = newSketch(context, id + "F4", { "sketchPlane" : qUnion([Q0])});
            skLineSegment(sketch, "E269.bottom", {"start": v(-264.16, -231.72) * mm, "end": v(429.84, -231.72) * mm});
            skLineSegment(sketch, "E269.top", {"start": v(-264.16, -234.72) * mm, "end": v(429.84, -234.72) * mm});
            skLineSegment(sketch, "E269.left", {"start": v(-264.16, -231.72) * mm, "end": v(-264.16, -234.72) * mm});
            skLineSegment(sketch, "E269.right", {"start": v(429.84, -231.72) * mm, "end": v(429.84, -234.72) * mm});
            skSolve(sketch);
        }
        {
            var Q0;
            Q0 = qSketchRegion(id + "F4", true);
            extrude(context, id + "F5", {"entities" : qUnion([Q0]), "operationType" : NewBodyOperationType.ADD, "oppositeDirection" : true, "depth" : 3 * mm});
        }
        {
            var Q0;
            Q0=makeQuery(id+"F1.opExtrude","CAP_FACE",FACE,{"disambiguationData":[OSD([sQuery(id+"F0.wireOp",EDGE,"E52"),sQuery(id+"F0.wireOp",EDGE,"E53"),sQuery(id+"F0.wireOp",EDGE,"E54"),sQuery(id+"F0.wireOp",EDGE,"E55"),sQuery(id+"F0.wireOp",EDGE,"E56"),sQuery(id+"F0.wireOp",EDGE,"E57"),sQuery(id+"F0.wireOp",EDGE,"E58"),sQuery(id+"F0.wireOp",EDGE,"E59"),sQuery(id+"F0.wireOp",EDGE,"E60"),sQuery(id+"F0.wireOp",EDGE,"E61"),sQuery(id+"F0.wireOp",EDGE,"E62"),sQuery(id+"F0.wireOp",EDGE,"E63"),sQuery(id+"F0.wireOp",EDGE,"E64"),sQuery(id+"F0.wireOp",EDGE,"E65"),sQuery(id+"F0.wireOp",EDGE,"E66"),sQuery(id+"F0.wireOp",EDGE,"E67"),sQuery(id+"F0.wireOp",EDGE,"E68"),sQuery(id+"F0.wireOp",EDGE,"E69"),sQuery(id+"F0.wireOp",EDGE,"E70"),sQuery(id+"F0.wireOp",EDGE,"E71"),sQuery(id+"F0.wireOp",EDGE,"E72"),sQuery(id+"F0.wireOp",EDGE,"E73"),sQuery(id+"F0.wireOp",EDGE,"E74"),sQuery(id+"F0.wireOp",EDGE,"E75"),sQuery(id+"F0.wireOp",EDGE,"E76"),sQuery(id+"F0.wireOp",EDGE,"E77"),sQuery(id+"F0.wireOp",EDGE,"E78"),sQuery(id+"F0.wireOp",EDGE,"E79"),sQuery(id+"F0.wireOp",EDGE,"E80"),sQuery(id+"F0.wireOp",EDGE,"E81"),sQuery(id+"F0.wireOp",EDGE,"E82"),sQuery(id+"F0.wireOp",EDGE,"E83"),sQuery(id+"F0.wireOp",EDGE,"E84"),sQuery(id+"F0.wireOp",EDGE,"E85"),sQuery(id+"F0.wireOp",EDGE,"E86"),sQuery(id+"F0.wireOp",EDGE,"E87"),sQuery(id+"F0.wireOp",EDGE,"E88"),sQuery(id+"F0.wireOp",EDGE,"E89"),sQuery(id+"F0.wireOp",EDGE,"E90"),sQuery(id+"F0.wireOp",EDGE,"E91"),sQuery(id+"F0.wireOp",EDGE,"E92"),sQuery(id+"F0.wireOp",EDGE,"E93"),sQuery(id+"F0.wireOp",EDGE,"E94"),sQuery(id+"F0.wireOp",EDGE,"E95"),sQuery(id+"F0.wireOp",EDGE,"E96"),sQuery(id+"F0.wireOp",EDGE,"E97"),sQuery(id+"F0.wireOp",EDGE,"E98"),sQuery(id+"F0.wireOp",EDGE,"E99"),sQuery(id+"F0.wireOp",EDGE,"E100"),sQuery(id+"F0.wireOp",EDGE,"E101"),sQuery(id+"F0.wireOp",EDGE,"E102"),sQuery(id+"F0.wireOp",EDGE,"E103"),sQuery(id+"F0.wireOp",EDGE,"E104"),sQuery(id+"F0.wireOp",EDGE,"E105"),sQuery(id+"F0.wireOp",EDGE,"E106"),sQuery(id+"F0.wireOp",EDGE,"E107"),sQuery(id+"F0.wireOp",EDGE,"E108"),sQuery(id+"F0.wireOp",EDGE,"E109"),sQuery(id+"F0.wireOp",EDGE,"E110"),sQuery(id+"F0.wireOp",EDGE,"E111"),sQuery(id+"F0.wireOp",EDGE,"E112"),sQuery(id+"F0.wireOp",EDGE,"E113"),sQuery(id+"F0.wireOp",EDGE,"E114"),sQuery(id+"F0.wireOp",EDGE,"E115"),sQuery(id+"F0.wireOp",EDGE,"E116"),sQuery(id+"F0.wireOp",EDGE,"E117"),sQuery(id+"F0.wireOp",EDGE,"E118"),sQuery(id+"F0.wireOp",EDGE,"E119"),sQuery(id+"F0.wireOp",EDGE,"E120"),sQuery(id+"F0.wireOp",EDGE,"E121"),sQuery(id+"F0.wireOp",EDGE,"E122"),sQuery(id+"F0.wireOp",EDGE,"E123"),sQuery(id+"F0.wireOp",EDGE,"E124"),sQuery(id+"F0.wireOp",EDGE,"E125"),sQuery(id+"F0.wireOp",EDGE,"E126"),sQuery(id+"F0.wireOp",EDGE,"E127"),sQuery(id+"F0.wireOp",EDGE,"E128"),sQuery(id+"F0.wireOp",EDGE,"E129"),sQuery(id+"F0.wireOp",EDGE,"E130"),sQuery(id+"F0.wireOp",EDGE,"E131"),sQuery(id+"F0.wireOp",EDGE,"E132"),sQuery(id+"F0.wireOp",EDGE,"E133"),sQuery(id+"F0.wireOp",EDGE,"E134"),sQuery(id+"F0.wireOp",EDGE,"E135"),sQuery(id+"F0.wireOp",EDGE,"E136"),sQuery(id+"F0.wireOp",EDGE,"E137"),sQuery(id+"F0.wireOp",EDGE,"E138"),sQuery(id+"F0.wireOp",EDGE,"E139"),sQuery(id+"F0.wireOp",EDGE,"E140"),sQuery(id+"F0.wireOp",EDGE,"E141"),sQuery(id+"F0.wireOp",EDGE,"E142"),sQuery(id+"F0.wireOp",EDGE,"E143"),sQuery(id+"F0.wireOp",EDGE,"E144"),sQuery(id+"F0.wireOp",EDGE,"E145"),sQuery(id+"F0.wireOp",EDGE,"E146"),sQuery(id+"F0.wireOp",EDGE,"E147"),sQuery(id+"F0.wireOp",EDGE,"E148"),sQuery(id+"F0.wireOp",EDGE,"E149"),sQuery(id+"F0.wireOp",EDGE,"E150"),sQuery(id+"F0.wireOp",EDGE,"E151"),sQuery(id+"F0.wireOp",EDGE,"E152"),sQuery(id+"F0.wireOp",EDGE,"E153"),sQuery(id+"F0.wireOp",EDGE,"E154"),sQuery(id+"F0.wireOp",EDGE,"E155"),sQuery(id+"F0.wireOp",EDGE,"E156"),sQuery(id+"F0.wireOp",EDGE,"E157"),sQuery(id+"F0.wireOp",EDGE,"E158"),sQuery(id+"F0.wireOp",EDGE,"E159"),sQuery(id+"F0.wireOp",EDGE,"E160"),sQuery(id+"F0.wireOp",EDGE,"E161"),sQuery(id+"F0.wireOp",EDGE,"E162"),sQuery(id+"F0.wireOp",EDGE,"E163"),sQuery(id+"F0.wireOp",EDGE,"E164"),sQuery(id+"F0.wireOp",EDGE,"E165"),sQuery(id+"F0.wireOp",EDGE,"E166"),sQuery(id+"F0.wireOp",EDGE,"E167")])],"isStart":false});
            var sketch = newSketch(context, id + "F6", { "sketchPlane" : qUnion([Q0])});
            skLineSegment(sketch, "E270.bottom", {"start": v(480.2, 231.72) * mm, "end": v(627.2, 231.72) * mm});
            skLineSegment(sketch, "E270.top", {"start": v(480.2, -62.28) * mm, "end": v(627.2, -62.28) * mm});
            skLineSegment(sketch, "E270.left", {"start": v(480.2, 231.72) * mm, "end": v(480.2, -62.28) * mm});
            skLineSegment(sketch, "E270.right", {"start": v(627.2, 231.72) * mm, "end": v(627.2, -62.28) * mm});
            skSolve(sketch);
        }
        {
            var Q0;
            Q0=makeQuery(id+"F6.imprint","IMPRINT",FACE,{"disambiguationData":[TD([[makeQuery(id+"F6.imprint","IMPRINT",EDGE,{"derivedFrom":sQuery(id+"F6.wireOp",EDGE,"E270.bottom")}),-1.0]])]});
            extrude(context, id + "F7", {"entities" : qUnion([Q0]), "oppositeDirection" : true, "depth" : 3 * mm});
        }
        {
            var Q0;
            Q0=makeQuery(id+"F7.opExtrude","CAP_FACE",FACE,{"disambiguationData":[OSD([sQuery(id+"F6.wireOp",EDGE,"E270.bottom"),sQuery(id+"F6.wireOp",EDGE,"E270.top"),sQuery(id+"F6.wireOp",EDGE,"E270.left"),sQuery(id+"F6.wireOp",EDGE,"E270.right")])],"isStart":true});
            var sketch = newSketch(context, id + "F8", { "sketchPlane" : qUnion([Q0])});
            skLineSegment(sketch, "E271.bottom", {"start": v(480.2, 197.22) * mm, "end": v(477.2, 197.22) * mm});
            skLineSegment(sketch, "E271.top", {"start": v(480.2, 159.72) * mm, "end": v(477.2, 159.72) * mm});
            skLineSegment(sketch, "E271.left", {"start": v(480.2, 197.22) * mm, "end": v(480.2, 159.72) * mm});
            skLineSegment(sketch, "E271.right", {"start": v(477.2, 197.22) * mm, "end": v(477.2, 159.72) * mm});
            skLineSegment(sketch, "E272.bottom", {"start": v(480.2, 129.72) * mm, "end": v(477.2, 129.72) * mm});
            skLineSegment(sketch, "E272.top", {"start": v(480.2, 99.72) * mm, "end": v(477.2, 99.72) * mm});
            skLineSegment(sketch, "E272.left", {"start": v(480.2, 129.72) * mm, "end": v(480.2, 99.72) * mm});
            skLineSegment(sketch, "E272.right", {"start": v(477.2, 129.72) * mm, "end": v(477.2, 99.72) * mm});
            skLineSegment(sketch, "E273.bottom", {"start": v(480.2, 69.72) * mm, "end": v(477.2, 69.72) * mm});
            skLineSegment(sketch, "E273.top", {"start": v(480.2, 39.72) * mm, "end": v(477.2, 39.72) * mm});
            skLineSegment(sketch, "E273.left", {"start": v(480.2, 69.72) * mm, "end": v(480.2, 39.72) * mm});
            skLineSegment(sketch, "E273.right", {"start": v(477.2, 69.72) * mm, "end": v(477.2, 39.72) * mm});
            skLineSegment(sketch, "E274.bottom", {"start": v(480.2, 9.72) * mm, "end": v(477.2, 9.72) * mm});
            skLineSegment(sketch, "E274.top", {"start": v(480.2, -27.78) * mm, "end": v(477.2, -27.78) * mm});
            skLineSegment(sketch, "E274.left", {"start": v(480.2, 9.72) * mm, "end": v(480.2, -27.78) * mm});
            skLineSegment(sketch, "E274.right", {"start": v(477.2, 9.72) * mm, "end": v(477.2, -27.78) * mm});
            skLineSegment(sketch, "E275.bottom", {"start": v(517.2, -62.28) * mm, "end": v(547.2, -62.28) * mm});
            skLineSegment(sketch, "E275.top", {"start": v(517.2, -65.28) * mm, "end": v(547.2, -65.28) * mm});
            skLineSegment(sketch, "E275.left", {"start": v(517.2, -62.28) * mm, "end": v(517.2, -65.28) * mm});
            skLineSegment(sketch, "E275.right", {"start": v(547.2, -62.28) * mm, "end": v(547.2, -65.28) * mm});
            skLineSegment(sketch, "E276.bottom", {"start": v(577.2, -62.28) * mm, "end": v(607.2, -62.28) * mm});
            skLineSegment(sketch, "E276.top", {"start": v(577.2, -65.28) * mm, "end": v(607.2, -65.28) * mm});
            skLineSegment(sketch, "E276.left", {"start": v(577.2, -62.28) * mm, "end": v(577.2, -65.28) * mm});
            skLineSegment(sketch, "E276.right", {"start": v(607.2, -62.28) * mm, "end": v(607.2, -65.28) * mm});
            skLineSegment(sketch, "E277", {"start": v(627.2, 84.72) * mm, "end": v(555.43, 84.72) * mm, "construction": true});
            skLineSegment(sketch, "E278.MirrorCS", {"start": v(547.2, 231.72) * mm, "end": v(547.2, 234.72) * mm});
            skLineSegment(sketch, "E279.MirrorCS", {"start": v(607.2, 231.72) * mm, "end": v(607.2, 234.72) * mm});
            skLineSegment(sketch, "E280.MirrorCS", {"start": v(577.2, 231.72) * mm, "end": v(577.2, 234.72) * mm});
            skLineSegment(sketch, "E281.MirrorCS", {"start": v(517.2, 231.72) * mm, "end": v(517.2, 234.72) * mm});
            skLineSegment(sketch, "E282.MirrorCS", {"start": v(577.2, 234.72) * mm, "end": v(607.2, 234.72) * mm});
            skLineSegment(sketch, "E283.MirrorCS", {"start": v(517.2, 234.72) * mm, "end": v(547.2, 234.72) * mm});
            skLineSegment(sketch, "E284.MirrorCS", {"start": v(517.2, 231.72) * mm, "end": v(547.2, 231.72) * mm});
            skLineSegment(sketch, "E285.MirrorCS", {"start": v(577.2, 231.72) * mm, "end": v(607.2, 231.72) * mm});
            skSolve(sketch);
        }
        {
            var Q0;
            Q0 = qSketchRegion(id + "F8", true);
            extrude(context, id + "F9", {"entities" : qUnion([Q0]), "operationType" : NewBodyOperationType.ADD, "oppositeDirection" : true, "depth" : 3 * mm});
        }
    });
